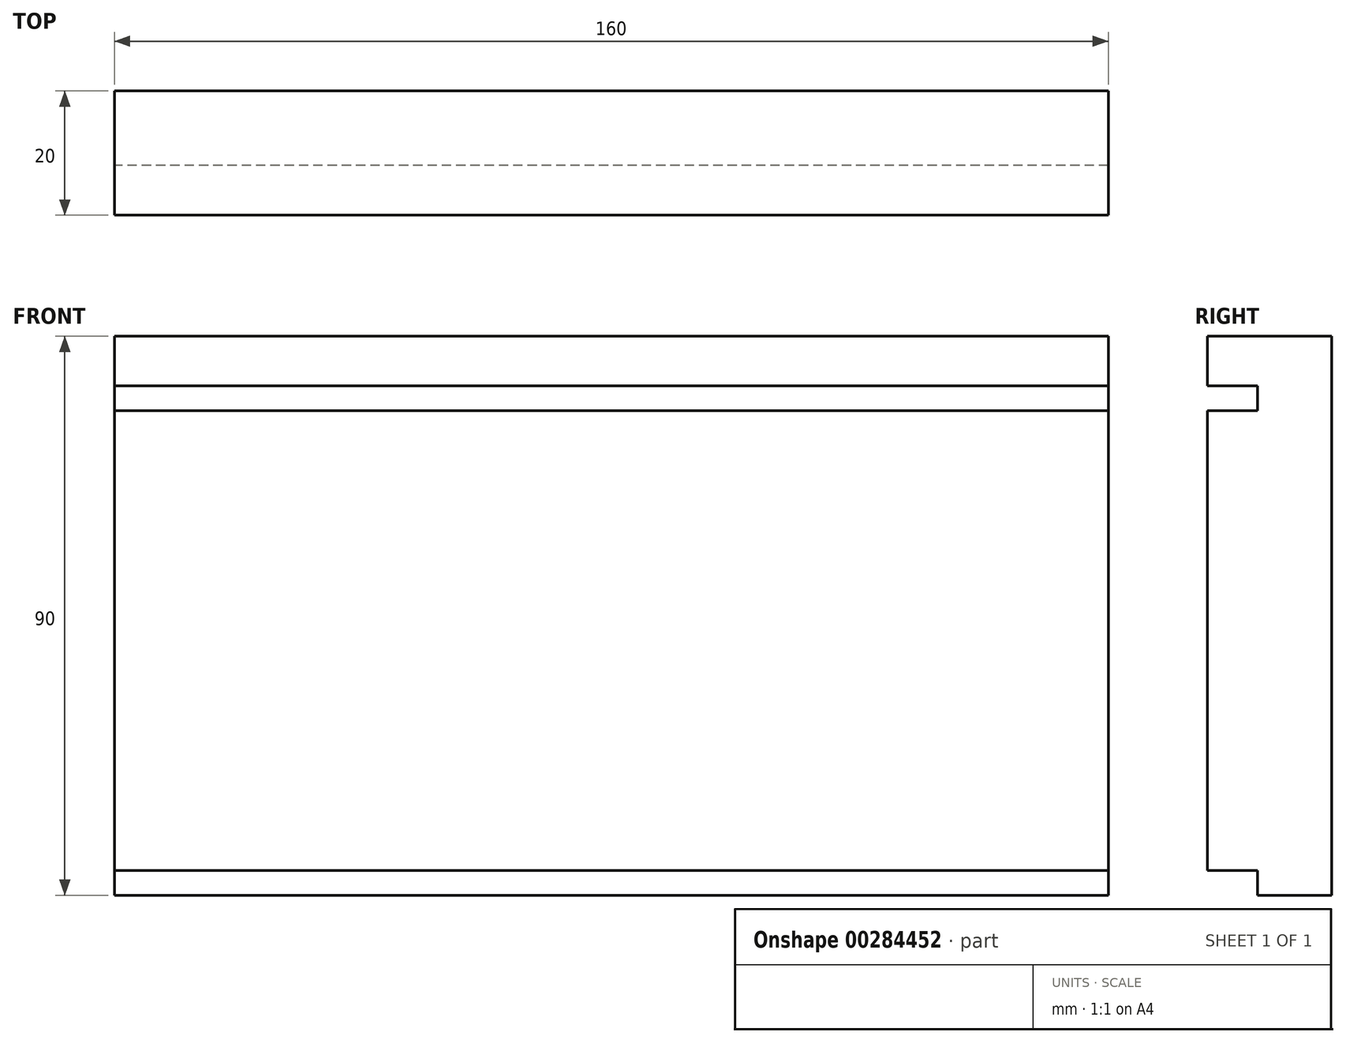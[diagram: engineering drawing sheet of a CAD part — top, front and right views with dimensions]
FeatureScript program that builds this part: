
annotation { "Feature Type Name" : "Feature", "Feature Type Description" : "" }
export const myFeature = defineFeature(function(context is Context, id is Id, definition is map)
    precondition{}
    {
        {
            var Q0;
            Q0=qCreatedBy(makeId("Front.planeOp"),FACE);
            var sketch = newSketch(context, id + "F0", { "sketchPlane" : qUnion([Q0])});
            skLineSegment(sketch, "E0.bottom", {"start": v(80, -45) * mm, "end": v(-80, -45) * mm});
            skLineSegment(sketch, "E0.top", {"start": v(80, 45) * mm, "end": v(-80, 45) * mm});
            skLineSegment(sketch, "E0.left", {"start": v(80, -45) * mm, "end": v(80, 45) * mm});
            skLineSegment(sketch, "E0.right", {"start": v(-80, -45) * mm, "end": v(-80, 45) * mm});
            skPoint(sketch, "E0.middle", {"position": v(0, 0) * mm});
            skLineSegment(sketch, "E1", {"start": v(-80, -41) * mm, "end": v(80, -41) * mm});
            skLineSegment(sketch, "E2", {"start": v(-80, 37) * mm, "end": v(80, 37) * mm});
            skLineSegment(sketch, "E3", {"start": v(80, 33) * mm, "end": v(-80, 33) * mm});
            skSolve(sketch);
        }
        {
            var Q0;
            {var subQ0=sQuery(id+"F0.wireOp",EDGE,"E0.top");Q0=makeQuery(id+"F0.imprint","IMPRINT",FACE,{"disambiguationData":[TD([[makeQuery(id+"F0.imprint","IMPRINT",EDGE,{"derivedFrom":subQ0}),1.0]])]});}
            var Q1;
            {var subQ0=sQuery(id+"F0.wireOp",EDGE,"E2");Q1=makeQuery(id+"F0.imprint","IMPRINT",FACE,{"disambiguationData":[TD([[makeQuery(id+"F0.imprint","IMPRINT",EDGE,{"derivedFrom":subQ0}),-1.0]])]});}
            var Q2;
            {var subQ0=sQuery(id+"F0.wireOp",EDGE,"E1");Q2=makeQuery(id+"F0.imprint","IMPRINT",FACE,{"disambiguationData":[TD([[makeQuery(id+"F0.imprint","IMPRINT",EDGE,{"derivedFrom":subQ0}),1.0]])]});}
            var Q3;
            {var subQ0=sQuery(id+"F0.wireOp",EDGE,"E0.bottom");Q3=makeQuery(id+"F0.imprint","IMPRINT",FACE,{"disambiguationData":[TD([[makeQuery(id+"F0.imprint","IMPRINT",EDGE,{"derivedFrom":subQ0}),-1.0]])]});}
            extrude(context, id + "F1", {"entities" : qUnion([Q0, Q1, Q2, Q3]), "depth" : 12 * mm});
        }
        {
            var Q0;
            {var subQ0=sQuery(id+"F0.wireOp",EDGE,"E0.top");Q0=makeQuery(id+"F0.imprint","IMPRINT",FACE,{"disambiguationData":[TD([[makeQuery(id+"F0.imprint","IMPRINT",EDGE,{"derivedFrom":subQ0}),1.0]])]});}
            var Q1;
            {var subQ0=sQuery(id+"F0.wireOp",EDGE,"E1");Q1=makeQuery(id+"F0.imprint","IMPRINT",FACE,{"disambiguationData":[TD([[makeQuery(id+"F0.imprint","IMPRINT",EDGE,{"derivedFrom":subQ0}),1.0]])]});}
            extrude(context, id + "F2", {"entities" : qUnion([Q0, Q1]), "operationType" : NewBodyOperationType.ADD, "depth" : 20 * mm});
        }
    });
